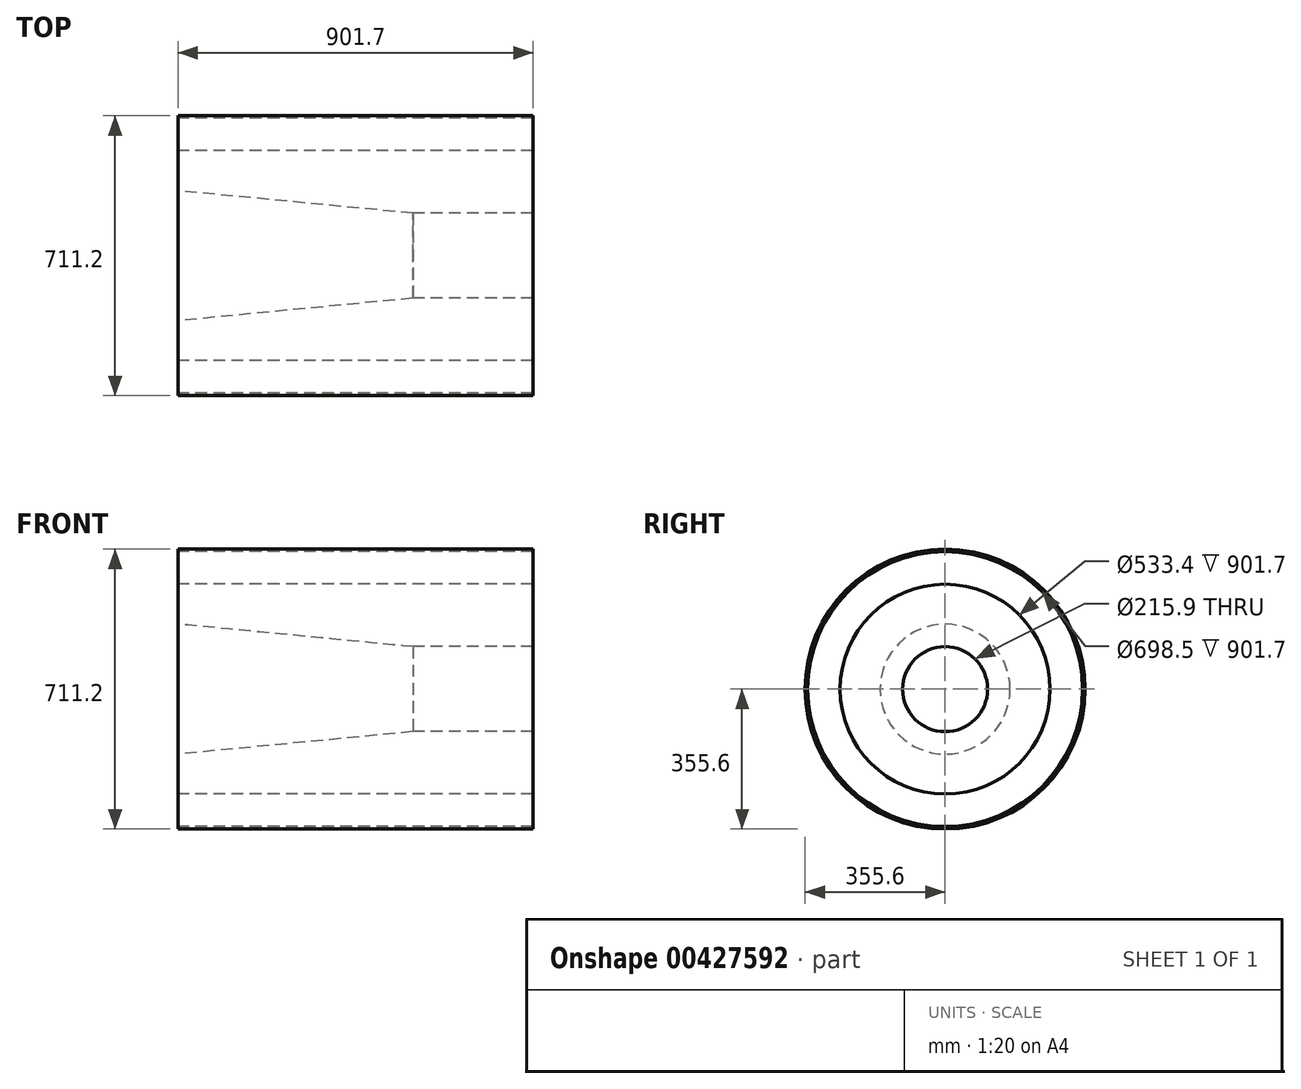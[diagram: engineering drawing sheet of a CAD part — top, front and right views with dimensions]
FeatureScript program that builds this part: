
annotation { "Feature Type Name" : "Feature", "Feature Type Description" : "" }
export const myFeature = defineFeature(function(context is Context, id is Id, definition is map)
    precondition{}
    {
        {
            var Q0;
            Q0=qCreatedBy(makeId("Front.planeOp"),FACE);
            var sketch = newSketch(context, id + "F0", { "sketchPlane" : qUnion([Q0])});
            skLineSegment(sketch, "E0", {"start": v(-90.9, 0) * mm, "end": v(89.4, 0) * mm, "construction": true});
            skLineSegment(sketch, "E1", {"start": v(0, 0) * mm, "end": v(0, 107.95) * mm});
            skLineSegment(sketch, "E2", {"start": v(0, 107.95) * mm, "end": v(0, 266.7) * mm});
            skPoint(sketch, "E3.endSnap0", {"position": v(0, 187.32) * mm});
            skLineSegment(sketch, "E4", {"start": v(0, 266.7) * mm, "end": v(0, 349.25) * mm});
            skLineSegment(sketch, "E5", {"start": v(0, 349.25) * mm, "end": v(0, 355.6) * mm});
            skLineSegment(sketch, "E6", {"start": v(0, 355.6) * mm, "end": v(-901.7, 355.6) * mm});
            skLineSegment(sketch, "E7", {"start": v(-901.7, 355.6) * mm, "end": v(-901.7, 349.25) * mm});
            skLineSegment(sketch, "E8", {"start": v(-901.7, 349.25) * mm, "end": v(-901.7, 266.7) * mm});
            skLineSegment(sketch, "E9", {"start": v(-901.7, 266.7) * mm, "end": v(-901.7, 165.1) * mm});
            skLineSegment(sketch, "E10", {"start": v(-901.7, 165.1) * mm, "end": v(-304.8, 107.95) * mm});
            skLineSegment(sketch, "E11", {"start": v(-304.8, 107.95) * mm, "end": v(0, 107.95) * mm});
            skLineSegment(sketch, "E12", {"start": v(-901.7, 266.7) * mm, "end": v(0, 266.7) * mm});
            skLineSegment(sketch, "E13", {"start": v(0, 349.25) * mm, "end": v(-901.7, 349.25) * mm});
            skSolve(sketch);
        }
        {
            var Q0;
            Q0=makeQuery(id+"F0.imprint","IMPRINT",FACE,{"disambiguationData":[TD([[makeQuery(id+"F0.imprint","IMPRINT",EDGE,{"derivedFrom":sQuery(id+"F0.wireOp",EDGE,"E5")}),1.0]])]});
            var Q1;
            Q1=sQuery(id+"F0.wireOp",EDGE,"E0");
            revolve(context, id + "F1", {"entities" : qUnion([Q0]), "axis" : qUnion([Q1]), "revolveType" : RevolveType.FULL});
        }
        {
            var Q0;
            Q0=makeQuery(id+"F0.imprint","IMPRINT",FACE,{"disambiguationData":[TD([[makeQuery(id+"F0.imprint","IMPRINT",EDGE,{"derivedFrom":sQuery(id+"F0.wireOp",EDGE,"E4")}),1.0]])]});
            var Q1;
            Q1=sQuery(id+"F0.wireOp",EDGE,"E0");
            revolve(context, id + "F2", {"entities" : qUnion([Q0]), "axis" : qUnion([Q1]), "revolveType" : RevolveType.FULL});
        }
        {
            var Q0;
            Q0=makeQuery(id+"F0.imprint","IMPRINT",FACE,{"disambiguationData":[TD([[makeQuery(id+"F0.imprint","IMPRINT",EDGE,{"derivedFrom":sQuery(id+"F0.wireOp",EDGE,"E2")}),1.0]])]});
            var Q1;
            Q1=sQuery(id+"F0.wireOp",EDGE,"E0");
            revolve(context, id + "F3", {"entities" : qUnion([Q0]), "axis" : qUnion([Q1]), "revolveType" : RevolveType.FULL});
        }
    });
